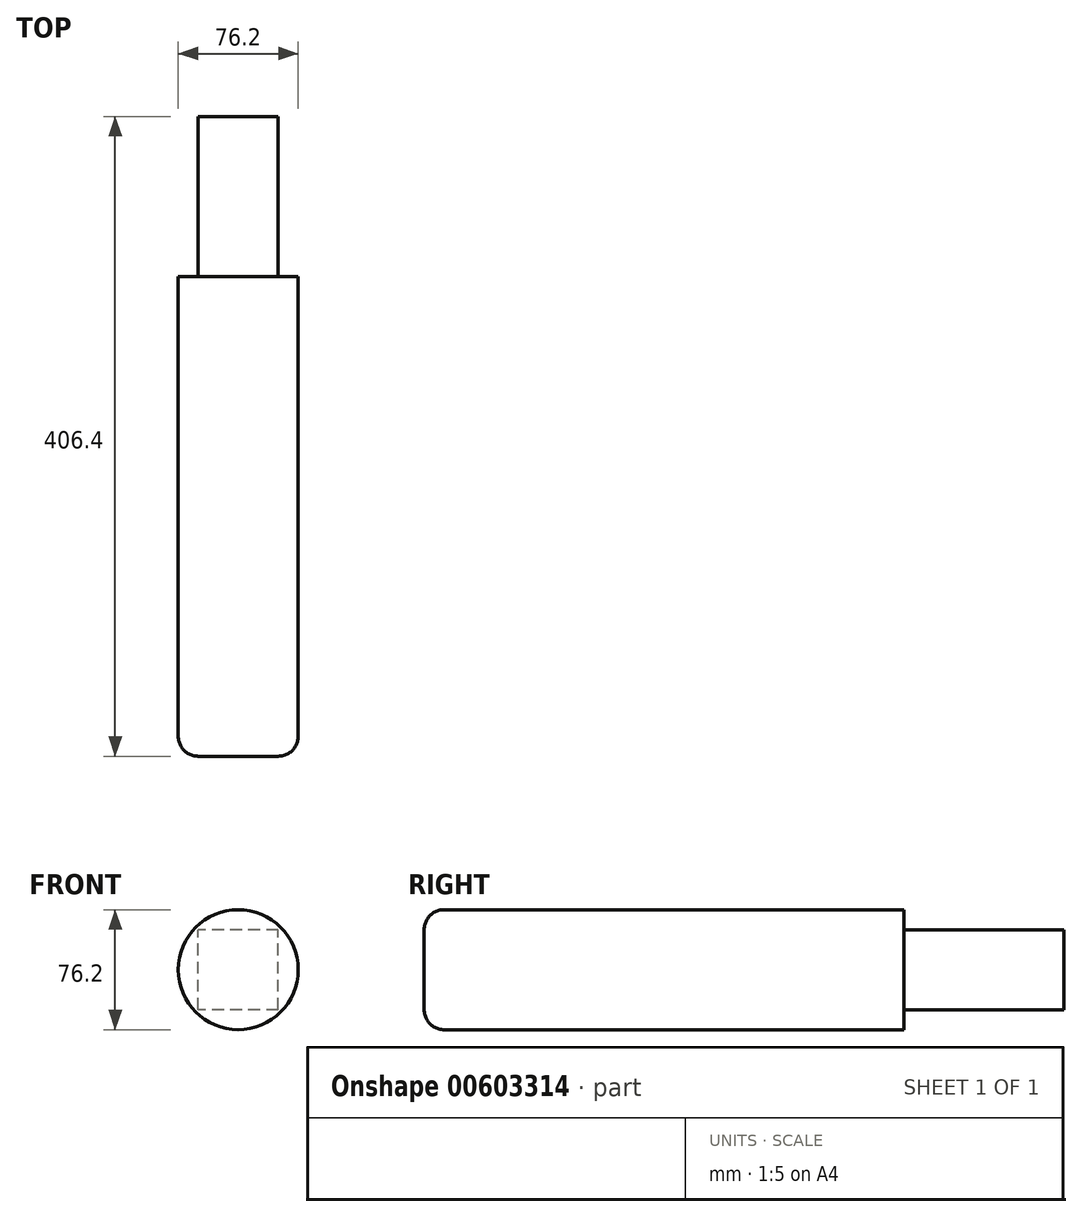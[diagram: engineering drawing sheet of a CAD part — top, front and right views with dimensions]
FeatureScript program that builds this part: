
annotation { "Feature Type Name" : "Feature", "Feature Type Description" : "" }
export const myFeature = defineFeature(function(context is Context, id is Id, definition is map)
    precondition{}
    {
        {
            var Q0;
            Q0=qCreatedBy(makeId("Front.planeOp"),FACE);
            var sketch = newSketch(context, id + "F0", { "sketchPlane" : qUnion([Q0])});
            skLineSegment(sketch, "E0.bottom", {"start": v(25.4, -25.4) * mm, "end": v(-25.4, -25.4) * mm});
            skLineSegment(sketch, "E0.top", {"start": v(25.4, 25.4) * mm, "end": v(-25.4, 25.4) * mm});
            skLineSegment(sketch, "E0.left", {"start": v(25.4, -25.4) * mm, "end": v(25.4, 25.4) * mm});
            skLineSegment(sketch, "E0.right", {"start": v(-25.4, -25.4) * mm, "end": v(-25.4, 25.4) * mm});
            skPoint(sketch, "E0.middle", {"position": v(0, 0) * mm});
            skSolve(sketch);
        }
        {
            var Q0;
            Q0=makeQuery(id+"F0.imprint","IMPRINT",FACE,{"disambiguationData":[TD([[makeQuery(id+"F0.imprint","IMPRINT",EDGE,{"derivedFrom":sQuery(id+"F0.wireOp",EDGE,"E0.bottom")}),-1.0]])]});
            extrude(context, id + "F1", {"entities" : qUnion([Q0]), "depth" : 101.6 * mm, "offsetDistance" : 25.4 * mm});
        }
        {
            var Q0;
            Q0=makeQuery(id+"F1.opExtrude","CAP_FACE",FACE,{"disambiguationData":[OSD([sQuery(id+"F0.wireOp",EDGE,"E0.bottom"),sQuery(id+"F0.wireOp",EDGE,"E0.top"),sQuery(id+"F0.wireOp",EDGE,"E0.left"),sQuery(id+"F0.wireOp",EDGE,"E0.right")])],"isStart":false});
            var sketch = newSketch(context, id + "F2", { "sketchPlane" : qUnion([Q0])});
            skCircle(sketch, "E1", {"center": v(0, 0) * mm, "radius": 38.1 * mm});
            skSolve(sketch);
        }
        {
            var Q0;
            Q0=makeQuery(id+"F2.imprint","IMPRINT",FACE,{"disambiguationData":[TD([[makeQuery(id+"F2.imprint","IMPRINT",EDGE,{"derivedFrom":sQuery(id+"F2.wireOp",EDGE,"E1")}),1.0]])]});
            var Q1;
            Q1=makeQuery(id+"F2.imprint","IMPRINT",FACE,{"disambiguationData":[TD([[makeQuery(id+"F2.imprint","IMPRINT",EDGE,{"derivedFrom":makeQuery(id+"F1.opExtrude","CAP_EDGE",EDGE,{"disambiguationData":[OSD([sQuery(id+"F0.wireOp",EDGE,"E0.bottom")])],"isStart":false})}),-1.0]])]});
            extrude(context, id + "F3", {"entities" : qUnion([Q0, Q1]), "operationType" : NewBodyOperationType.ADD, "depth" : 304.8 * mm, "offsetDistance" : 25.4 * mm});
        }
        {
            var Q0;
            Q0=makeQuery(id+"F3.opExtrude","CAP_EDGE",EDGE,{"disambiguationData":[OSD([sQuery(id+"F2.wireOp",EDGE,"E1")])],"isStart":false});
            fillet(context, id + "F4", {"entities" : qUnion([Q0]), "radius" : 12.7 * mm, "tangentPropagation" : true, "allowEdgeOverflow" : false});
        }
    });
